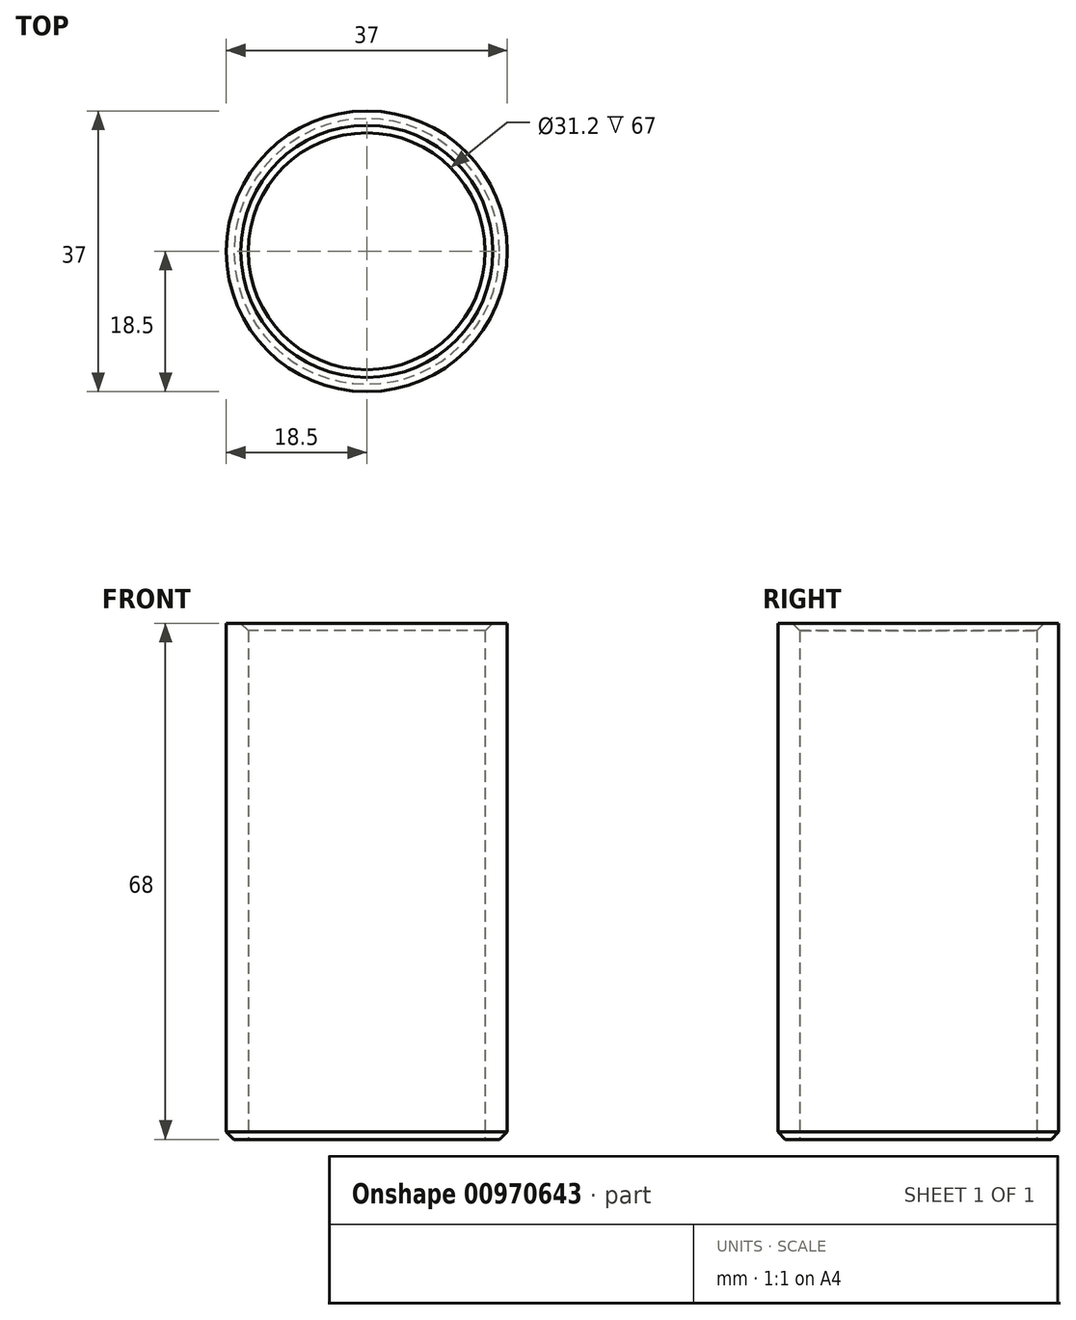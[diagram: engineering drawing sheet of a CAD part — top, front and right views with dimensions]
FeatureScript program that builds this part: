
annotation { "Feature Type Name" : "Feature", "Feature Type Description" : "" }
export const myFeature = defineFeature(function(context is Context, id is Id, definition is map)
    precondition{}
    {
        {
            var Q0;
            Q0=qCreatedBy(makeId("Top.planeOp"),FACE);
            var sketch = newSketch(context, id + "F0", { "sketchPlane" : qUnion([Q0])});
            skCircle(sketch, "E0", {"center": v(0, 0) * mm, "radius": 18.5 * mm});
            skSolve(sketch);
        }
        {
            var Q0;
            Q0 = qSketchRegion(id + "F0", true);
            extrude(context, id + "F1", {"entities" : qUnion([Q0]), "depth" : 68 * mm, "offsetDistance" : 25 * mm});
        }
        {
            var Q0;
            Q0=qCreatedBy(makeId("Top.planeOp"),FACE);
            var sketch = newSketch(context, id + "F2", { "sketchPlane" : qUnion([Q0])});
            skCircle(sketch, "E1", {"center": v(0, 0) * mm, "radius": 15.6 * mm});
            skSolve(sketch);
        }
        {
            var Q0;
            Q0 = qSketchRegion(id + "F2", true);
            extrude(context, id + "F3", {"entities" : qUnion([Q0]), "operationType" : NewBodyOperationType.REMOVE, "endBound" : BoundingType.THROUGH_ALL, "depth" : 25 * mm, "offsetDistance" : 25 * mm});
        }
        {
            var Q0;
            Q0=makeQuery(id+"F1.opExtrude","CAP_EDGE",EDGE,{"disambiguationData":[OSD([sQuery(id+"F0.wireOp",EDGE,"E0")])],"isStart":true});
            chamfer(context, id + "F4", {"entities" : qUnion([Q0]), "width" : 1 * mm, "tangentPropagation" : true});
        }
        {
            var Q0;
            Q0=makeQuery(id+"F3.boolean.opBoolean","INTERSECT",EDGE,{"derivedFrom":[makeQuery(id+"F1.opExtrude","CAP_FACE",FACE,{"disambiguationData":[OSD([sQuery(id+"F0.wireOp",EDGE,"E0")])],"isStart":false}),makeQuery(id+"F3.opExtrude","SWEPT_FACE",FACE,{"disambiguationData":[OSD([sQuery(id+"F2.wireOp",EDGE,"E1")])]})]});
            chamfer(context, id + "F5", {"entities" : qUnion([Q0]), "width" : 1 * mm, "tangentPropagation" : true});
        }
    });
